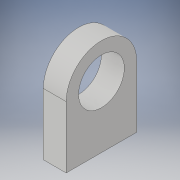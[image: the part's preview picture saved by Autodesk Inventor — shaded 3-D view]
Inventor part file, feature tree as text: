
AUTODESK INVENTOR PART (.ipt)
format: ipt  version: 2017 (Build 210142000, 142)  size: 100,352 bytes
history: native  units: in
note: dims shown in document units (in); Inventor stores cm internally (conversion verified against a paired STEP export)
features: extrude x1, sketch x1
ambient origin geometry x8: Origin, YZ Plane, XZ Plane, XY Plane, X Axis, Y Axis, Z Axis, Center Point
bodies: Solid1 (feature_tree)
feature tree (2):
  extrude  "Extrusion1"  Depth=0.77in
  sketch  "Sketch1"  dims[d0=0.5in d1=0.77in d2=0.675in d3=0.675in d4=0.25in d5=0.0in]
